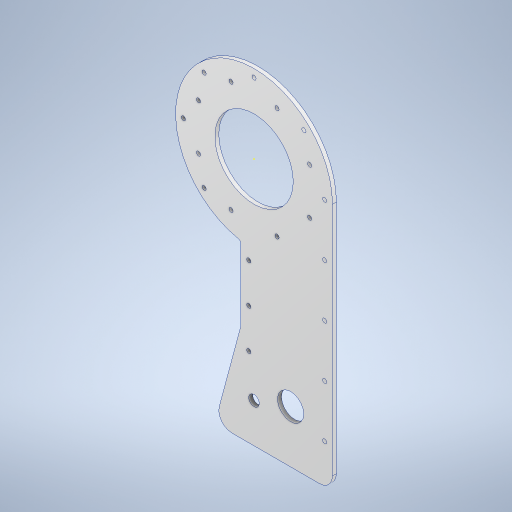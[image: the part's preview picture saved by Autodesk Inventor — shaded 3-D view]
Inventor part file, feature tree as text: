
AUTODESK INVENTOR PART (.ipt)
format: ipt  version: 2024.3 (Build 283343000, 343)  size: 421,376 bytes
history: native  units: mm
features: sketch x9, extrude x4, hole x4, fillet x2, other x1
ambient origin geometry x8: Origin, YZ Plane, XZ Plane, XY Plane, X Axis, Y Axis, Z Axis, Center Point
bodies: Body1 (feature_tree)
feature tree (20):
  other  "ソリッド1"
  extrude  "押し出し1"  Depth=120.0mm
  hole  "穴1"  [1 undecoded]
  extrude  "押し出し3"  Depth=92.0mm
  extrude  "押し出し10"  TaperAngle=22.5deg  [1 undecoded]
  hole  "穴8"  [1 undecoded]
  fillet  "フィレット4"  Radius=60.0mm
  hole  "穴13"  [1 undecoded]
  hole  "穴14"  [1 undecoded]
  fillet  "フィレット11"  Radius=190.0mm
  sketch  "スケッチ30"
  extrude  "押し出し16"  Depth=3.0mm TaperAngle=0.0deg
  sketch  "スケッチ1"
  sketch  "スケッチ2"
  sketch  "スケッチ4"
  sketch  "スケッチ17"
  sketch  "スケッチ20"
  sketch  "スケッチ28"
  sketch  "スケッチ29"
  sketch  "スケッチ32"
note: 5 required parameter values undecoded (feature->parameter linkage not recoverable at this tier; creation-order binding heuristic only, values carry confidence <= 0.55)
